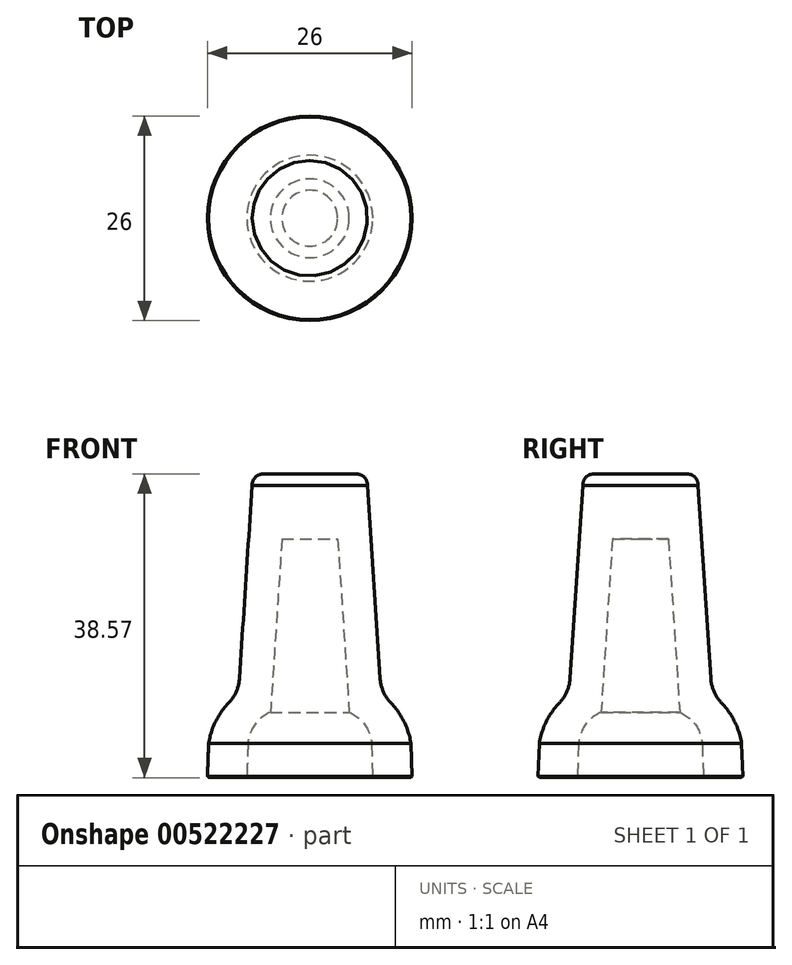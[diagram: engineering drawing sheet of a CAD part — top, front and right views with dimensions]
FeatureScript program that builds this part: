
annotation { "Feature Type Name" : "Feature", "Feature Type Description" : "" }
export const myFeature = defineFeature(function(context is Context, id is Id, definition is map)
    precondition{}
    {
        {
            var Q0;
            Q0=qCreatedBy(makeId("Right.planeOp"),FACE);
            var sketch = newSketch(context, id + "F0", { "sketchPlane" : qUnion([Q0])});
            skLineSegment(sketch, "E0", {"start": v(12.83, -38.57) * mm, "end": v(8, -38.57) * mm});
            skLineSegment(sketch, "E1", {"start": v(8, -38.57) * mm, "end": v(7.85, -34.37) * mm});
            skLineSegment(sketch, "E2", {"start": v(5, -30.27) * mm, "end": v(3.55, -8.27) * mm});
            skLineSegment(sketch, "E3", {"start": v(3.55, -8.27) * mm, "end": v(0, -8.27) * mm});
            skLineSegment(sketch, "E4", {"start": v(0, -8.27) * mm, "end": v(0, 0) * mm});
            skPoint(sketch, "E5.visualSharp", {"position": v(7.66, -28.75) * mm});
            skLineSegment(sketch, "E6", {"start": v(5, -30.27) * mm, "end": v(16.73, -30.27) * mm, "construction": true});
            skArc(sketch, "E7", {"start": v(7.85, -34.37) * mm, "mid": v(7.03, -31.9) * mm, "end": v(5, -30.27) * mm});
            skLineSegment(sketch, "E8.0", {"start": v(9.07, -28) * mm, "end": v(7.32, -1.46) * mm});
            skArc(sketch, "E8.1", {"start": v(12.85, -34.2) * mm, "mid": v(11.57, -30.73) * mm, "end": v(9.07, -28) * mm});
            skLineSegment(sketch, "E8.2", {"start": v(13, -38.4) * mm, "end": v(12.85, -34.2) * mm});
            skLineSegment(sketch, "E9", {"start": v(13, -38.4) * mm, "end": v(12.83, -38.57) * mm});
            skLineSegment(sketch, "E10", {"start": v(5.95, 0) * mm, "end": v(0, 0) * mm});
            skPoint(sketch, "E11.visualSharp", {"position": v(7.22, 0) * mm});
            skArc(sketch, "E12", {"start": v(7.32, -1.46) * mm, "mid": v(6.95, -0.43) * mm, "end": v(5.95, 0) * mm});
            skSolve(sketch);
        }
        {
            var Q0;
            Q0=makeQuery(id+"F0.imprint","IMPRINT",FACE,{"disambiguationData":[TD([[makeQuery(id+"F0.imprint","IMPRINT",EDGE,{"derivedFrom":sQuery(id+"F0.wireOp",EDGE,"E0")}),-1.0]])]});
            var Q1;
            Q1=sQuery(id+"F0.wireOp",EDGE,"E4");
            revolve(context, id + "F1", {"entities" : qUnion([Q0]), "axis" : qUnion([Q1]), "revolveType" : RevolveType.FULL});
        }
        {
            var Q0;
            Q0=makeQuery(id+"F1.opRevolve","SWEPT_EDGE",EDGE,{"disambiguationData":[OSD([sQuery(id+"F0.wireOp",EDGE,"E8.0"),sQuery(id+"F0.wireOp",EDGE,"E8.1")])]});
            fillet(context, id + "F2", {"entities" : qUnion([Q0]), "radius" : 5 * mm, "tangentPropagation" : true, "allowEdgeOverflow" : false});
        }
    });
